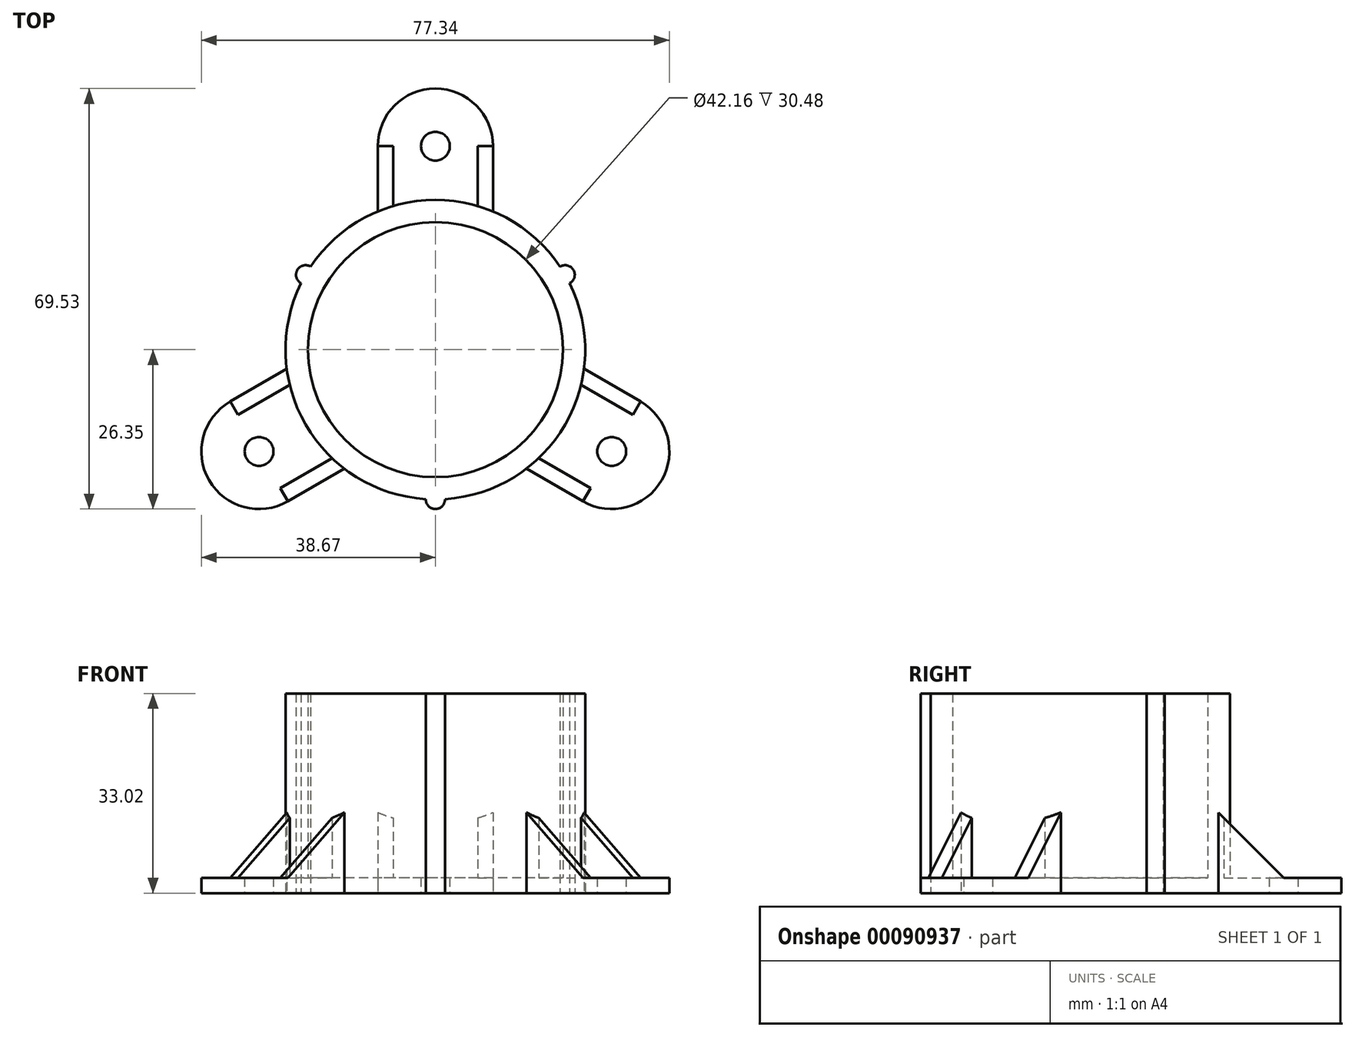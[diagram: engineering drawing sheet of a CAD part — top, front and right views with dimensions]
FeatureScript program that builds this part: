
annotation { "Feature Type Name" : "Feature", "Feature Type Description" : "" }
export const myFeature = defineFeature(function(context is Context, id is Id, definition is map)
    precondition{}
    {
        {
            var Q0;
            Q0=qCreatedBy(makeId("Top.planeOp"),FACE);
            var sketch = newSketch(context, id + "F0", { "sketchPlane" : qUnion([Q0])});
            skCircle(sketch, "E0", {"center": v(0, 0) * mm, "radius": 21.08 * mm});
            skCircle(sketch, "E1", {"center": v(0, 0) * mm, "radius": 24.77 * mm});
            skCircle(sketch, "E2", {"center": v(0, -24.77) * mm, "radius": 1.59 * mm});
            skCircle(sketch, "E3.1.0", {"center": v(21.45, 12.38) * mm, "radius": 1.59 * mm});
            skCircle(sketch, "E3.2.0", {"center": v(-21.45, 12.38) * mm, "radius": 1.59 * mm});
            skLineSegment(sketch, "E4.bottom", {"start": v(-9.53, 22.86) * mm, "end": v(9.53, 22.86) * mm});
            skLineSegment(sketch, "E4.top", {"start": v(0, 43.18) * mm, "end": v(0, 43.18) * mm});
            skLineSegment(sketch, "E4.left", {"start": v(-9.53, 22.86) * mm, "end": v(-9.53, 33.66) * mm});
            skLineSegment(sketch, "E4.right", {"start": v(9.52, 22.86) * mm, "end": v(9.52, 33.66) * mm});
            skLineSegment(sketch, "E5", {"start": v(0, 13) * mm, "end": v(0, 41.76) * mm, "construction": true});
            skPoint(sketch, "E6.visualSharp", {"position": v(-9.53, 43.18) * mm});
            skArc(sketch, "E6.filletArc", {"start": v(0, 43.18) * mm, "mid": v(-6.74, 40.4) * mm, "end": v(-9.53, 33.66) * mm});
            skPoint(sketch, "E7.visualSharp", {"position": v(9.53, 43.18) * mm});
            skArc(sketch, "E7.filletArc", {"start": v(9.53, 33.66) * mm, "mid": v(6.74, 40.4) * mm, "end": v(0, 43.18) * mm});
            skCircle(sketch, "E8", {"center": v(0, 33.66) * mm, "radius": 2.38 * mm});
            skArc(sketch, "E9.1.0", {"start": v(-33.9, -8.58) * mm, "mid": v(-38.35, -14.36) * mm, "end": v(-37.4, -21.59) * mm});
            skArc(sketch, "E9.1.1", {"start": v(-37.4, -21.6) * mm, "mid": v(-31.61, -26.03) * mm, "end": v(-24.38, -25.08) * mm});
            skCircle(sketch, "E9.1.2", {"center": v(-29.15, -16.83) * mm, "radius": 2.38 * mm});
            skLineSegment(sketch, "E9.1.3", {"start": v(-24.56, -3.18) * mm, "end": v(-33.9, -8.58) * mm});
            skLineSegment(sketch, "E9.1.4", {"start": v(-15.03, -19.68) * mm, "end": v(-24.38, -25.08) * mm});
            skLineSegment(sketch, "E9.1.5", {"start": v(-15.03, -19.68) * mm, "end": v(-24.56, -3.18) * mm});
            skArc(sketch, "E9.2.0", {"start": v(24.38, -25.08) * mm, "mid": v(31.61, -26.03) * mm, "end": v(37.4, -21.6) * mm});
            skArc(sketch, "E9.2.1", {"start": v(37.4, -21.6) * mm, "mid": v(38.35, -14.36) * mm, "end": v(33.9, -8.58) * mm});
            skCircle(sketch, "E9.2.2", {"center": v(29.15, -16.83) * mm, "radius": 2.38 * mm});
            skLineSegment(sketch, "E9.2.3", {"start": v(15.03, -19.68) * mm, "end": v(24.38, -25.08) * mm});
            skLineSegment(sketch, "E9.2.4", {"start": v(24.56, -3.18) * mm, "end": v(33.9, -8.58) * mm});
            skLineSegment(sketch, "E9.2.5", {"start": v(24.56, -3.18) * mm, "end": v(15.03, -19.68) * mm});
            skSolve(sketch);
        }
        {
            var Q0;
            Q0 = qSketchRegion(id + "F0", true);
            var Q1;
            Q1=makeQuery(id+"F0.imprint","IMPRINT",FACE,{"disambiguationData":[TD([[makeQuery(id+"F0.imprint","IMPRINT",EDGE,{"derivedFrom":sQuery(id+"F0.wireOp",EDGE,"E0")}),1.0]])]});
            extrude(context, id + "F1", {"entities" : qUnion([Q0, Q1]), "depth" : 2.54 * mm});
        }
        {
            var Q0;
            Q0=makeQuery(id+"F0.imprint","IMPRINT",FACE,{"disambiguationData":[TD([[makeQuery(id+"F0.imprint","IMPRINT",EDGE,{"derivedFrom":sQuery(id+"F0.wireOp",EDGE,"E0")}),-1.0]])]});
            var Q1;
            {var subQ0=sQuery(id+"F0.wireOp",EDGE,"E9.1.5");Q1=makeQuery(id+"F0.imprint","IMPRINT",FACE,{"disambiguationData":[TD([[makeQuery(id+"F0.imprint","IMPRINT",EDGE,{"derivedFrom":subQ0}),1.0]])]});}
            var Q2;
            {var subQ0=sQuery(id+"F0.wireOp",EDGE,"E3.2.0");var subQ1=sQuery(id+"F0.wireOp",EDGE,"E1");var subQ2=makeQuery(id+"F0.imprint","INTERSECT",VERTEX,{"disambiguationData":[OD(0.0)],"derivedFrom":[subQ1,subQ0]});Q2=makeQuery(id+"F0.imprint","IMPRINT",FACE,{"disambiguationData":[TD([[makeQuery(id+"F0.imprint","IMPRINT",EDGE,{"disambiguationData":[TD([[subQ2,-1.0]])],"derivedFrom":subQ1}),1.0]])]});}
            var Q3;
            {var subQ0=sQuery(id+"F0.wireOp",EDGE,"E3.2.0");var subQ1=sQuery(id+"F0.wireOp",EDGE,"E1");var subQ2=makeQuery(id+"F0.imprint","INTERSECT",VERTEX,{"disambiguationData":[OD(0.0)],"derivedFrom":[subQ1,subQ0]});Q3=makeQuery(id+"F0.imprint","IMPRINT",FACE,{"disambiguationData":[TD([[makeQuery(id+"F0.imprint","IMPRINT",EDGE,{"disambiguationData":[TD([[subQ2,-1.0]])],"derivedFrom":subQ1}),-1.0]])]});}
            var Q4;
            {var subQ0=sQuery(id+"F0.wireOp",EDGE,"E3.1.0");var subQ1=sQuery(id+"F0.wireOp",EDGE,"E1");var subQ2=makeQuery(id+"F0.imprint","INTERSECT",VERTEX,{"disambiguationData":[OD(0.0)],"derivedFrom":[subQ1,subQ0]});Q4=makeQuery(id+"F0.imprint","IMPRINT",FACE,{"disambiguationData":[TD([[makeQuery(id+"F0.imprint","IMPRINT",EDGE,{"disambiguationData":[TD([[subQ2,1.0]])],"derivedFrom":subQ1}),1.0]])]});}
            var Q5;
            {var subQ0=sQuery(id+"F0.wireOp",EDGE,"E3.1.0");var subQ1=sQuery(id+"F0.wireOp",EDGE,"E1");var subQ2=makeQuery(id+"F0.imprint","INTERSECT",VERTEX,{"disambiguationData":[OD(0.0)],"derivedFrom":[subQ1,subQ0]});Q5=makeQuery(id+"F0.imprint","IMPRINT",FACE,{"disambiguationData":[TD([[makeQuery(id+"F0.imprint","IMPRINT",EDGE,{"disambiguationData":[TD([[subQ2,1.0]])],"derivedFrom":subQ1}),-1.0]])]});}
            var Q6;
            {var subQ0=sQuery(id+"F0.wireOp",EDGE,"E2");var subQ1=sQuery(id+"F0.wireOp",EDGE,"E1");var subQ2=makeQuery(id+"F0.imprint","INTERSECT",VERTEX,{"disambiguationData":[OD(0.0)],"derivedFrom":[subQ1,subQ0]});Q6=makeQuery(id+"F0.imprint","IMPRINT",FACE,{"disambiguationData":[TD([[makeQuery(id+"F0.imprint","IMPRINT",EDGE,{"disambiguationData":[TD([[subQ2,-1.0]])],"derivedFrom":subQ1}),-1.0]])]});}
            var Q7;
            {var subQ0=sQuery(id+"F0.wireOp",EDGE,"E2");var subQ1=sQuery(id+"F0.wireOp",EDGE,"E1");var subQ2=makeQuery(id+"F0.imprint","INTERSECT",VERTEX,{"disambiguationData":[OD(0.0)],"derivedFrom":[subQ1,subQ0]});Q7=makeQuery(id+"F0.imprint","IMPRINT",FACE,{"disambiguationData":[TD([[makeQuery(id+"F0.imprint","IMPRINT",EDGE,{"disambiguationData":[TD([[subQ2,-1.0]])],"derivedFrom":subQ1}),1.0]])]});}
            var Q8;
            {var subQ0=sQuery(id+"F0.wireOp",EDGE,"E4.bottom");Q8=makeQuery(id+"F0.imprint","IMPRINT",FACE,{"disambiguationData":[TD([[makeQuery(id+"F0.imprint","IMPRINT",EDGE,{"derivedFrom":subQ0}),1.0]])]});}
            var Q9;
            {var subQ0=sQuery(id+"F0.wireOp",EDGE,"E9.2.5");Q9=makeQuery(id+"F0.imprint","IMPRINT",FACE,{"disambiguationData":[TD([[makeQuery(id+"F0.imprint","IMPRINT",EDGE,{"derivedFrom":subQ0}),1.0]])]});}
            extrude(context, id + "F2", {"entities" : qUnion([Q0, Q1, Q2, Q3, Q4, Q5, Q6, Q7, Q8, Q9]), "operationType" : NewBodyOperationType.ADD, "depth" : 33.02 * mm});
        }
        {
            var Q0;
            Q0=makeQuery(id+"F1.opExtrude","SWEPT_FACE",FACE,{"disambiguationData":[OSD([sQuery(id+"F0.wireOp",EDGE,"E4.right")])]});
            var sketch = newSketch(context, id + "F3", { "sketchPlane" : qUnion([Q0])});
            skLineSegment(sketch, "E10.0", {"start": v(22.86, 2.54) * mm, "end": v(33.66, 2.54) * mm});
            skLineSegment(sketch, "E11", {"start": v(22.86, 2.54) * mm, "end": v(22.86, 13.33) * mm});
            skLineSegment(sketch, "E12", {"start": v(22.86, 13.33) * mm, "end": v(33.66, 2.54) * mm});
            skSolve(sketch);
        }
        {
            var Q0;
            Q0 = qSketchRegion(id + "F3", true);
            extrude(context, id + "F4", {"entities" : qUnion([Q0]), "oppositeDirection" : true, "depth" : 2.54 * mm});
        }
        {
            var Q0;
            Q0=makeQuery(id+"F4.opExtrude","SWEPT_BODY",BODY,{"disambiguationData":[OSD([sQuery(id+"F3.wireOp",EDGE,"E10.0"),sQuery(id+"F3.wireOp",EDGE,"E11"),sQuery(id+"F3.wireOp",EDGE,"E12")])]});
            var Q1;
            Q1=qCreatedBy(makeId("Right.planeOp"),FACE);
            mirror(context, id + "F5", {"entities" : qUnion([Q0]), "mirrorPlane" : qUnion([Q1])});
        }
        {
            var Q0;
            Q0=makeQuery(id+"F4.opExtrude","SWEPT_BODY",BODY,{"disambiguationData":[OSD([sQuery(id+"F3.wireOp",EDGE,"E10.0"),sQuery(id+"F3.wireOp",EDGE,"E11"),sQuery(id+"F3.wireOp",EDGE,"E12")])]});
            var Q1;
            Q1=makeQuery(id+"F5.opPattern","COPY",BODY,{"derivedFrom":makeQuery(id+"F4.opExtrude","SWEPT_BODY",BODY,{"disambiguationData":[OSD([sQuery(id+"F3.wireOp",EDGE,"E10.0"),sQuery(id+"F3.wireOp",EDGE,"E11"),sQuery(id+"F3.wireOp",EDGE,"E12")])]}),"instanceName":"1"});
            var Q2;
            Q2=makeQuery(id+"F2.boolean.opBoolean","INTERSECT",EDGE,{"derivedFrom":[makeQuery(id+"F1.opExtrude","CAP_FACE",FACE,{"disambiguationData":[OSD([sQuery(id+"F0.wireOp",EDGE,"E1"),sQuery(id+"F0.wireOp",EDGE,"E2"),sQuery(id+"F0.wireOp",EDGE,"E3.1.0"),sQuery(id+"F0.wireOp",EDGE,"E3.2.0"),sQuery(id+"F0.wireOp",EDGE,"E4.left"),sQuery(id+"F0.wireOp",EDGE,"E4.right"),sQuery(id+"F0.wireOp",EDGE,"E6.filletArc"),sQuery(id+"F0.wireOp",EDGE,"E7.filletArc"),sQuery(id+"F0.wireOp",EDGE,"E8"),sQuery(id+"F0.wireOp",EDGE,"E9.1.0"),sQuery(id+"F0.wireOp",EDGE,"E9.1.1"),sQuery(id+"F0.wireOp",EDGE,"E9.1.2"),sQuery(id+"F0.wireOp",EDGE,"E9.1.3"),sQuery(id+"F0.wireOp",EDGE,"E9.1.4"),sQuery(id+"F0.wireOp",EDGE,"E9.2.0"),sQuery(id+"F0.wireOp",EDGE,"E9.2.1"),sQuery(id+"F0.wireOp",EDGE,"E9.2.2"),sQuery(id+"F0.wireOp",EDGE,"E9.2.3"),sQuery(id+"F0.wireOp",EDGE,"E9.2.4")])],"isStart":false}),makeQuery(id+"F2.opExtrude","SWEPT_FACE",FACE,{"disambiguationData":[OSD([sQuery(id+"F0.wireOp",EDGE,"E0")])]})]});
            circularPattern(context, id + "F6", {"operationType" : NewBodyOperationType.ADD, "entities" : qUnion([Q0, Q1]), "axis" : qUnion([Q2]), "angle" : 120 * degree, "instanceCount" : 3});
        }
    });
